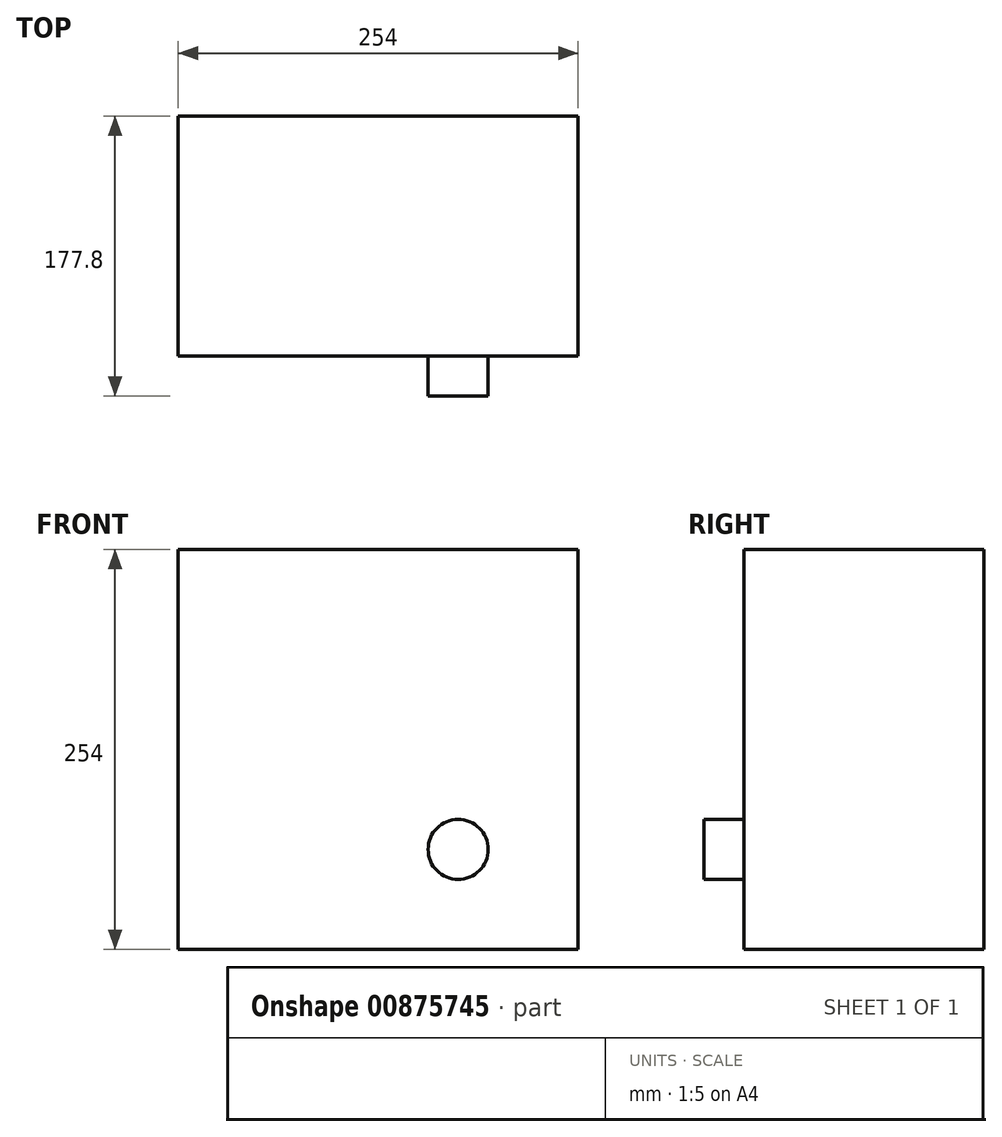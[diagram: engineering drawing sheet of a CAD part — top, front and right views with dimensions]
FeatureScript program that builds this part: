
annotation { "Feature Type Name" : "Feature", "Feature Type Description" : "" }
export const myFeature = defineFeature(function(context is Context, id is Id, definition is map)
    precondition{}
    {
        {
            var Q0;
            Q0=qCreatedBy(makeId("Front.planeOp"),FACE);
            var sketch = newSketch(context, id + "F0", { "sketchPlane" : qUnion([Q0])});
            skLineSegment(sketch, "E0.bottom", {"start": v(127, 127) * mm, "end": v(-127, 127) * mm});
            skLineSegment(sketch, "E0.top", {"start": v(127, -127) * mm, "end": v(-127, -127) * mm});
            skLineSegment(sketch, "E0.left", {"start": v(127, 127) * mm, "end": v(127, -127) * mm});
            skLineSegment(sketch, "E0.right", {"start": v(-127, 127) * mm, "end": v(-127, -127) * mm});
            skPoint(sketch, "E0.middle", {"position": v(0, 0) * mm});
            skSolve(sketch);
        }
        {
            var Q0;
            Q0=makeQuery(id+"F0.imprint","IMPRINT",FACE,{"disambiguationData":[TD([[makeQuery(id+"F0.imprint","IMPRINT",EDGE,{"derivedFrom":sQuery(id+"F0.wireOp",EDGE,"E0.bottom")}),1.0]])]});
            extrude(context, id + "F1", {"entities" : qUnion([Q0]), "depth" : 152.4 * mm, "offsetDistance" : 25.4 * mm});
        }
        {
            var Q0;
            Q0=makeQuery(id+"F1.opExtrude","CAP_FACE",FACE,{"disambiguationData":[OSD([sQuery(id+"F0.wireOp",EDGE,"E0.bottom"),sQuery(id+"F0.wireOp",EDGE,"E0.top"),sQuery(id+"F0.wireOp",EDGE,"E0.left"),sQuery(id+"F0.wireOp",EDGE,"E0.right")])],"isStart":false});
            var sketch = newSketch(context, id + "F2", { "sketchPlane" : qUnion([Q0])});
            skLineSegment(sketch, "E1.bottom", {"start": v(0, 0) * mm, "end": v(101.6, 0) * mm});
            skLineSegment(sketch, "E1.top", {"start": v(0, 101.6) * mm, "end": v(101.6, 101.6) * mm});
            skLineSegment(sketch, "E1.left", {"start": v(0, 0) * mm, "end": v(0, 101.6) * mm});
            skLineSegment(sketch, "E1.right", {"start": v(101.6, 0) * mm, "end": v(101.6, 101.6) * mm});
            skCircle(sketch, "E2", {"center": v(50.8, -63.5) * mm, "radius": 19.05 * mm});
            skSolve(sketch);
        }
        {
            var Q0;
            Q0=makeQuery(id+"F2.imprint","IMPRINT",FACE,{"disambiguationData":[TD([[makeQuery(id+"F2.imprint","IMPRINT",EDGE,{"derivedFrom":sQuery(id+"F2.wireOp",EDGE,"E2")}),1.0]])]});
            extrude(context, id + "F3", {"entities" : qUnion([Q0]), "depth" : 25.4 * mm, "offsetDistance" : 25.4 * mm});
        }
    });
